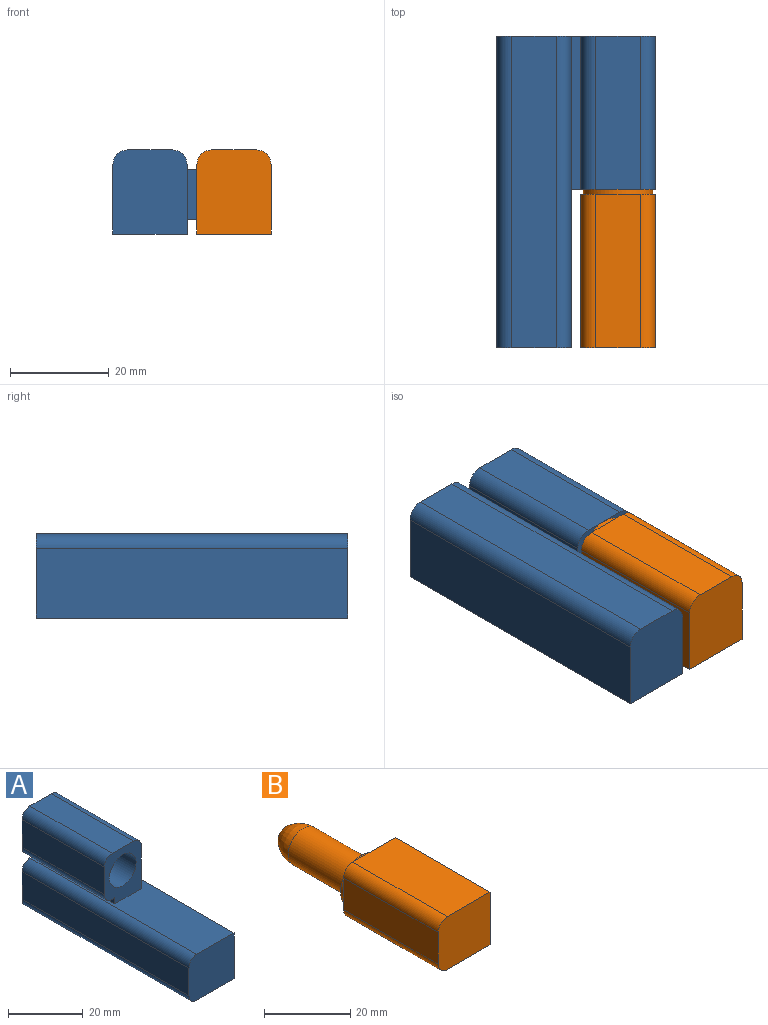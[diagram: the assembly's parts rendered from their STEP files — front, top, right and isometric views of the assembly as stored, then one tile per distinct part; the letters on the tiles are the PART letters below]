
ASSEMBLY  parts=2 mates=1
PART A: 28 faces, bbox 17x63x32 mm
  f0: cylinder r=3mm len=63mm, axis (0,-1,0), area 296.9mm2, adj f1,f13,f14,f15
  f1: plane 63x9mm, normal (-1,0,0), area 567mm2, adj f0,f2,f14,f15
  f2: cylinder r=3mm len=63mm, axis (0,-1,0), area 296.9mm2, adj f1,f11,f14,f15
  f3: plane 31x2mm, normal (-1,0,0), area 62mm2, adj f4,f11,f14,f16
  f4: plane 31x1mm, normal (0,0,-1), area 31mm2, adj f3,f5,f14,f16
  f5: cylinder r=3mm len=31mm, axis (0,-1,0), area 146.1mm2, adj f4,f6,f14,f16
  f6: plane 31x9mm, normal (-1,0,0), area 279mm2, adj f5,f7,f14,f16
  f7: cylinder r=3mm len=31mm, axis (0,-1,0), area 146.1mm2, adj f6,f8,f14,f16
  f8: plane 31x8mm, normal (0,0,1), area 248mm2, adj f7,f9,f14,f16
  f9: cylinder r=3mm len=31mm, axis (0,-1,0), area 146.1mm2, adj f8,f10,f14,f16
  f10: plane 31x14mm, normal (1,0,0), area 434mm2, adj f9,f11,f14,f16
  f11: plane 63x14mm, normal (0,0,1), area 572mm2, adj f2,f3,f10,f12,f14,f15,f16
  f12: plane 63x15mm, normal (1,0,0), area 897.5mm2, adj f11,f13,f14,f15,f20,f24
  f13: plane 63x14mm, normal (0,0,-1), area 882mm2, adj f0,f12,f14,f15
  f14: plane 32x17mm, normal (0,1,0), area 475.3mm2, adj f0,f1,f2,f3,f4,f5,f6,f7
  f15: plane 17x15mm, normal (0,-1,0), area 251.1mm2, adj f0,f1,f2,f11,f12,f13
  f16: plane 17x14mm, normal (0,-1,0), area 144.1mm2, adj f3,f4,f5,f6,f7,f8,f9,f10
  f17: cylinder r=5.05mm len=28mm, axis (0,1,0), area 888.4mm2, adj f16,f18
  f18: torus R=4.55mm, axis (0,1,0), area 24mm2, adj f17,f19
  f19: plane 9.1x9.1mm, normal (0,-1,0), area 65mm2, adj f18
  f20: cylinder r=2.75mm len=5.5mm, axis (-1,0,0), area 8.6mm2, adj f12,f21
  f21: cone r=2.75mm half-angle=31.1deg, axis (1,0,0), area 20mm2, adj f20,f22
  f22: cylinder r=2.07mm len=11.37mm, axis (-1,0,0), area 147.7mm2, adj f21,f23
  f23: cone r=2.07mm half-angle=60deg, axis (1,0,0), area 15.5mm2, adj f22
  f24: cylinder r=2.75mm len=5.5mm, axis (-1,0,0), area 8.6mm2, adj f12,f25
  f25: cone r=2.75mm half-angle=31.1deg, axis (1,0,0), area 20mm2, adj f24,f26
  f26: cylinder r=2.07mm len=11.37mm, axis (-1,0,0), area 147.7mm2, adj f25,f27
  f27: cone r=2.07mm half-angle=60deg, axis (1,0,0), area 15.5mm2, adj f26
PART B: 21 faces, bbox 17x57x15 mm
  f0: cylinder r=3mm len=31mm, axis (0,1,0), area 146.1mm2, adj f1,f5,f6,f7
  f1: plane 31x9mm, normal (-1,0,0), area 279mm2, adj f0,f2,f6,f7
  f2: cylinder r=3mm len=31mm, axis (0,1,0), area 146.1mm2, adj f1,f3,f6,f7
  f3: plane 31x14mm, normal (0,0,1), area 434mm2, adj f2,f4,f6,f7
  f4: plane 31x15mm, normal (1,0,0), area 417.5mm2, adj f3,f5,f6,f7,f13,f17
  f5: plane 31x14mm, normal (0,0,-1), area 434mm2, adj f0,f4,f6,f7
  f6: plane 17x15mm, normal (0,-1,0), area 251.1mm2, adj f0,f1,f2,f3,f4,f5
  f7: plane 17x15mm, normal (0,1,0), area 97.2mm2, adj f0,f1,f2,f3,f4,f5,f8
  f8: cylinder r=7mm len=14mm, axis (0,1,0), area 44mm2, adj f7,f9
  f9: plane 14x14mm, normal (0,1,0), area 75.4mm2, adj f8,f10
  f10: cylinder r=5mm len=19.19mm, axis (0,1,0), area 602.9mm2, adj f9,f11
  f11: revolved ~10x10mm, area 169.5mm2, adj f10,f12
  f12: plane 5x5mm, normal (0,1,0), area 19.6mm2, adj f11
  f13: cylinder r=2.75mm len=5.5mm, axis (-1,0,0), area 8.6mm2, adj f4,f14
  f14: cone r=2.75mm half-angle=31.1deg, axis (1,0,0), area 20mm2, adj f13,f15
  f15: cylinder r=2.07mm len=11.37mm, axis (-1,0,0), area 147.7mm2, adj f14,f16
  f16: cone r=2.07mm half-angle=60deg, axis (1,0,0), area 15.5mm2, adj f15
  f17: cylinder r=2.75mm len=5.5mm, axis (-1,0,0), area 8.6mm2, adj f4,f18
  f18: cone r=2.75mm half-angle=31.1deg, axis (1,0,0), area 20mm2, adj f17,f19
  f19: cylinder r=2.07mm len=11.37mm, axis (-1,0,0), area 147.7mm2, adj f18,f20
  f20: cone r=2.07mm half-angle=60deg, axis (1,0,0), area 15.5mm2, adj f19
PLACE A rot(axis=(0,1,0),90deg) t=(-11.6,-23.72,20.97)mm
PLACE B rot(axis=(0,1,0),90deg) t=(-11.6,7.28,20.97)mm
MATE revolute B.f8 <-> A.f17  axis (0,1,0) through (-11.6,8.28,30.97)mm
